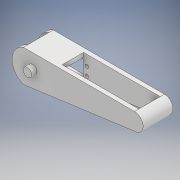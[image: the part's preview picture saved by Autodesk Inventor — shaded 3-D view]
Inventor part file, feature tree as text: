
AUTODESK INVENTOR PART (.ipt)
format: ipt  version: 2018 (Build 220112000, 112)  size: 177,664 bytes
history: native  units: mm
features: extrude x7, sketch x7, plane x1, mirror x1
ambient origin geometry x8: Origin, YZ Plane, XZ Plane, XY Plane, X Axis, Y Axis, Z Axis, Center Point
bodies: Solid1 (feature_tree)
feature tree (16):
  extrude  "Extrusion1"  Depth=20.0mm
  sketch  "Sketch5"  dims[d3=20.0mm d4=5.0mm d5=0.0mm]
  extrude  "Extrusion3"  Depth=5.0mm TaperAngle=0.0deg
  plane  "Work Plane1"
  mirror  "Mirror1"
  extrude  "Extrusion4"  Depth=20.0mm
  extrude  "Extrusion6"  TaperAngle=0.0deg  [1 undecoded]
  extrude  "Extrusion7"  Depth=5.0mm
  extrude  "Extrusion10"  Depth=5.0mm TaperAngle=0.0deg
  extrude  "Extrusion11"  Depth=5.0mm TaperAngle=0.0deg
  sketch  "Sketch1"  dims[d0=130.0mm d1=20.0mm]
  sketch  "Sketch8"  dims[d13=40.3mm d14=20.0mm]
  sketch  "Sketch11"  dims[d15=7.0mm d16=0.0mm]
  sketch  "Sketch14"  dims[d17=5.0mm d18=0.0mm d19=12.5mm]
  sketch  "Sketch17"  dims[d20=5.0mm d21=0.0mm d29=5.0mm d30=0.0mm]
  sketch  "Sketch18"  dims[d31=40.0mm d32=5.0mm d33=0.0mm d38=34.75mm d39=0.0mm d40=6.0mm d41=0.0mm d42=10.0mm]
note: 1 required parameter value undecoded (feature->parameter linkage not recoverable at this tier; creation-order binding heuristic only, values carry confidence <= 0.55)
